# Revit family: Навес теневой тип 5 Арт 12758
name_source: partatom
category: Антураж
revit_build: Autodesk Revit 2018 (Build: 20180423_1000(x64)
units: mm (PartAtom-declared; Revit-internal decimal feet)

## family parameters
Всегда вертикально = Да
Источник визуального образа = Геометрия семейства
На основе рабочей плоскости = Нет
Общий = Нет
При загрузке вырезать с полостями = Нет
Точка расчета площади = Нет

## types (3) — shared parameters
URL = https://hobbyka.ru
Артикул товара = Арт. 12758
Высота = 2800 мм
Группа модели = Навесы и беседки
Длина = 5000 мм
Изготовитель = ООО «Хоббика»
Изображение типоразмера = Навес теневой тип 5 Арт 12758.jpg
Материал изделия = Сталь, дерево
Цвет каркаса = Сталь черная
Цвет отделки = Дерево
Ширина = 2000 мм

## per-type parameters (varying)
| type | Описание | Полный комплект | Стенка |
| Навес теневой Тип 5. Полный сомплект | Навес теневой Тип 5. Комплект со стенкой, скамейкой и урной | Да | Нет |
| Навес теневой Тип 5. Со стенкой | Навес теневой Тип 5. Комплект со стенкой | Нет | Да |
| Навес теневой Тип 5 | Навес теневой Тип 5 | Нет | Нет |
